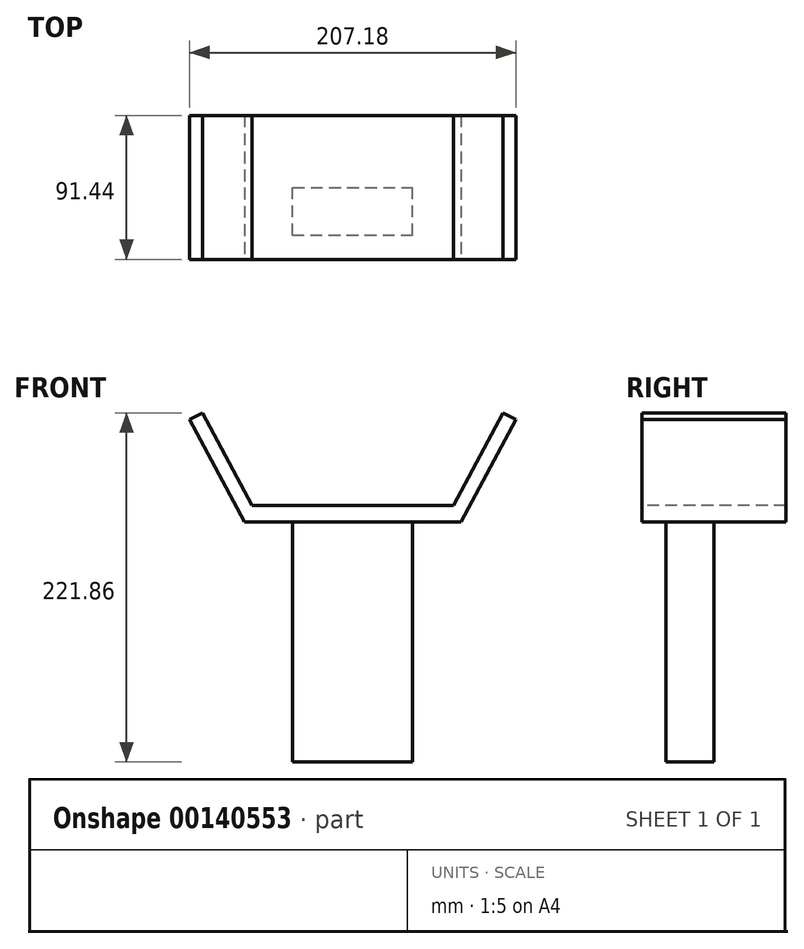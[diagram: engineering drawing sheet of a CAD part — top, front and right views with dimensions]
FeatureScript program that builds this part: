
annotation { "Feature Type Name" : "Feature", "Feature Type Description" : "" }
export const myFeature = defineFeature(function(context is Context, id is Id, definition is map)
    precondition{}
    {
        {
            var Q0;
            Q0=qCreatedBy(makeId("Top.planeOp"),FACE);
            var sketch = newSketch(context, id + "F0", { "sketchPlane" : qUnion([Q0])});
            skLineSegment(sketch, "E0.bottom", {"start": v(-38.1, -15.24) * mm, "end": v(38.1, -15.24) * mm});
            skLineSegment(sketch, "E0.top", {"start": v(-38.1, 15.24) * mm, "end": v(38.1, 15.24) * mm});
            skLineSegment(sketch, "E0.left", {"start": v(-38.1, -15.24) * mm, "end": v(-38.1, 15.24) * mm});
            skLineSegment(sketch, "E0.right", {"start": v(38.1, -15.24) * mm, "end": v(38.1, 15.24) * mm});
            skPoint(sketch, "E0.middle", {"position": v(0, 0) * mm});
            skSolve(sketch);
        }
        {
            var Q0;
            Q0 = qSketchRegion(id + "F0", true);
            extrude(context, id + "F1", {"entities" : qUnion([Q0]), "depth" : 152.4 * mm});
        }
        {
            var Q0;
            Q0=makeQuery(id+"F1.opExtrude","SWEPT_FACE",FACE,{"disambiguationData":[OSD([sQuery(id+"F0.wireOp",EDGE,"E0.bottom")])]});
            var sketch = newSketch(context, id + "F2", { "sketchPlane" : qUnion([Q0])});
            skLineSegment(sketch, "E1", {"start": v(-38.1, 152.4) * mm, "end": v(-68.7, 152.4) * mm});
            skLineSegment(sketch, "E2", {"start": v(-68.7, 152.4) * mm, "end": v(-103.6, 217.54) * mm});
            skLineSegment(sketch, "E3", {"start": v(-103.6, 217.54) * mm, "end": v(-95.53, 221.86) * mm});
            skLineSegment(sketch, "E4", {"start": v(-95.53, 221.86) * mm, "end": v(-64.1, 163.16) * mm});
            skLineSegment(sketch, "E5", {"start": v(-64.1, 163.16) * mm, "end": v(0, 163.16) * mm});
            skLineSegment(sketch, "E6", {"start": v(0, 0) * mm, "end": v(0, 57.71) * mm, "construction": true});
            skLineSegment(sketch, "E7.MirrorCS", {"start": v(64.1, 163.16) * mm, "end": v(0, 163.16) * mm});
            skLineSegment(sketch, "E8.MirrorCS", {"start": v(103.6, 217.54) * mm, "end": v(95.53, 221.86) * mm});
            skLineSegment(sketch, "E9.MirrorCS", {"start": v(95.53, 221.86) * mm, "end": v(64.1, 163.16) * mm});
            skLineSegment(sketch, "E10.MirrorCS", {"start": v(38.1, 152.4) * mm, "end": v(68.7, 152.4) * mm});
            skLineSegment(sketch, "E11.MirrorCS", {"start": v(68.7, 152.4) * mm, "end": v(103.6, 217.54) * mm});
            skSolve(sketch);
        }
        {
            var Q0;
            Q0=makeQuery(id+"F2.imprint","IMPRINT",FACE,{"disambiguationData":[TD([[makeQuery(id+"F2.imprint","IMPRINT",EDGE,{"derivedFrom":sQuery(id+"F2.wireOp",EDGE,"E1")}),-1.0]])]});
            extrude(context, id + "F3", {"entities" : qUnion([Q0]), "operationType" : NewBodyOperationType.ADD, "oppositeDirection" : true, "depth" : 76.2 * mm});
        }
        {
            var Q0;
            Q0=makeQuery(id+"F2.imprint","IMPRINT",FACE,{"disambiguationData":[TD([[makeQuery(id+"F2.imprint","IMPRINT",EDGE,{"derivedFrom":sQuery(id+"F2.wireOp",EDGE,"E1")}),-1.0]])]});
            extrude(context, id + "F4", {"entities" : qUnion([Q0]), "operationType" : NewBodyOperationType.ADD, "depth" : 15.24 * mm});
        }
    });
